# Revit family: MV-3T - Top Inlet
name_source: partatom
category: Mechanical Equipment
revit_build: Autodesk Revit 2018 (Build: 20170223_1515(x64)
units: mm (PartAtom-declared; Revit-internal decimal feet)

## family parameters
Always vertical = Yes
Cut with Voids When Loaded = No
OmniClass Number = 23.75.00.00
OmniClass Title = Climate Control (HVAC)
Part Type = Normal
Room Calculation Point = No
Round Connector Dimension = Use Radius
Shared = No
Work Plane-Based = No

## types (19) — shared parameters
Manufacturer = Anemostat
Model = MV-3T (Top Inlet)
URL = http://www.anemostat-hvac.com

## per-type parameters (varying)
| type | CenterH | CenterV | Diff Length | Diff Width | Duct Radius | Duct Size | Inlet Radius | Inlet Size | Module Length | Module Width | Plenum Length |
| MV-3T - 24x48, 18" Round Top Inlet | 11 7/8" | 23 7/8" | 47 3/4" | 23 3/4" | 9" | 18" | 9" | 18" | 48" | 24" | 43 5/16" |
| MV-3T - 8x24, 5" Round Top Inlet | 3 7/8" | 11 7/8" | 23 3/4" | 7 3/4" | 2" | 5" | 2" | 5" | 24" | 8" | 21 5/16" |
| MV-3T - 24x36, 18" Round Top Inlet | 11 7/8" | 17 7/8" | 35 3/4" | 23 3/4" | 9" | 18" | 9" | 18" | 36" | 24" | 31 5/16" |
| MV-3T - 24x60, 18" Round Top Inlet | 11 7/8" | 29 7/8" | 59 3/4" | 23 3/4" | 9" | 18" | 9" | 18" | 60" | 24" | 55 5/16" |
| MV-3T - 24x72, 18" Round Top Inlet | 11 7/8" | 35 7/8" | 71 3/4" | 23 3/4" | 9" | 18" | 9" | 18" | 72" | 24" | 67 5/16" |
| MV-3T - 36x72, 18" Round Top Inlet | 17 7/8" | 35 7/8" | 71 3/4" | 35 3/4" | 9" | 18" | 9" | 18" | 72" | 36" | 67 5/16" |
| MV-3T - 36x60, 18" Round Top Inlet | 17 7/8" | 29 7/8" | 59 3/4" | 35 3/4" | 9" | 18" | 9" | 18" | 60" | 36" | 55 5/16" |
| MV-3T -36x48, 18" Round Top Inlet | 17 7/8" | 23 7/8" | 47 3/4" | 35 3/4" | 9" | 18" | 9" | 18" | 48" | 36" | 43 5/16" |
| MV-3T -36x36, 18" Round Top Inlet | 17 7/8" | 17 7/8" | 35 3/4" | 35 3/4" | 9" | 18" | 9" | 18" | 36" | 36" | 31 5/16" |
| MV-3T - 12x48, 9" Round Top Inlet | 5 7/8" | 23 7/8" | 47 3/4" | 11 3/4" | 4" | 9" | 4" | 9" | 48" | 12" | 43 5/16" |
| MV-3T - 12x60, 9" Round Top Inlet | 5 7/8" | 29 7/8" | 59 3/4" | 11 3/4" | 4" | 9" | 4" | 9" | 60" | 12" | 55 5/16" |
| MV-3T - 12x72, 9" Round Top Inlet | 5 7/8" | 35 7/8" | 71 3/4" | 11 3/4" | 4" | 9" | 4" | 9" | 72" | 12" | 67 5/16" |
| MV-3T - 12x36, 9" Round Top Inlet | 5 7/8" | 17 7/8" | 35 3/4" | 11 3/4" | 4" | 9" | 4" | 9" | 36" | 12" | 31 5/16" |
| MV-3T- 12x24, 9" Round Top Inlet | 5 7/8" | 11 7/8" | 23 3/4" | 11 3/4" | 4" | 9" | 4" | 9" | 24" | 12" | 21 5/16" |
| MV-3T - 24x24, 18" Round Top Inlet | 11 7/8" | 11 7/8" | 23 3/4" | 23 3/4" | 9" | 18" | 9" | 18" | 24" | 24" | 31 5/16" |
| MV-3T - 8x72, 5" Round Top Inlet | 3 7/8" | 35 7/8" | 71 3/4" | 7 3/4" | 2" | 5" | 2" | 5" | 72" | 8" | 67 5/16" |
| MV-3T - 8x36, 5" Round Top Inlet | 3 7/8" | 17 7/8" | 35 3/4" | 7 3/4" | 2" | 5" | 2" | 5" | 36" | 8" | 21 5/16" |
| MV-3T - 8x48, 5" Round Top Inlet | 3 7/8" | 23 7/8" | 47 3/4" | 7 3/4" | 2" | 5" | 2" | 5" | 48" | 8" | 21 5/16" |
| MV-3T - 8x60, 5" Round Top Inlet | 3 7/8" | 29 7/8" | 59 3/4" | 7 3/4" | 2" | 5" | 2" | 5" | 60" | 8" | 21 5/16" |

## geometry (parser evidence)
native form markers: Sweep x2
no freeform markers — native parametric forms only
